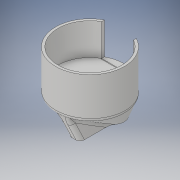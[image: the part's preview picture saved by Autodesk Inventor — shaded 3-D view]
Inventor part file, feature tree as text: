
AUTODESK INVENTOR PART (.ipt)
format: ipt  version: 2019 (Build 230136000, 136)  size: 461,824 bytes
history: native  units: mm
features: sketch x7, extrude x5, fillet x5, loft x2, other x2, plane x1
ambient origin geometry x8: Origin, YZ Plane, XZ Plane, XY Plane, X Axis, Y Axis, Z Axis, Center Point
bodies: Solid1 (feature_tree)
feature tree (22):
  extrude  "Extrusion1"  Depth=86.0mm
  extrude  "Extrusion2"  Depth=1.0mm
  extrude  "Extrusion3"  Depth=40.0mm
  sketch  "Sketch9"  dims[d7=80.0mm d8=10.0mm d9=0.0mm]
  plane  "Work Plane2"
  loft  "Loft1"
  extrude  "Extrusion6"  Depth=40.0mm
  loft  "Loft2"
  fillet  "Fillet1"  [1 undecoded]
  fillet  "Fillet2"  Radius=20.0mm
  extrude  "Extrusion8"  TaperAngle=0.0deg  [1 undecoded]
  fillet  "Fillet4"  [1 undecoded]
  fillet  "Fillet5"  Radius=10.0mm
  fillet  "Fillet6"  Radius=10.0mm
  sketch  "Sketch1"  dims[d0=80.0mm d1=86.0mm]
  sketch  "Sketch2"  dims[d2=40.0mm d3=0.0mm d4=1.0mm]
  sketch  "Sketch3"  dims[d5=1.0mm d6=40.0mm]
  sketch  "Sketch10"  dims[d10=10.0mm d11=0.0mm d21=40.0mm]
  sketch  "Sketch11"  dims[d22=26.0mm d23=0.0mm d24=90.0deg d25=0.0mm d26=90.0deg d27=20.0mm]
  other  "Edges1"
  other  "Edges2"
  sketch  "Sketch12"  dims[d28=20.0mm d29=0.0mm d30=0.0mm d31=90.0deg d32=0.0mm d33=90.0deg d34=10.0mm d35=10.0mm d36=86.0mm d37=86.0mm d38=43.0mm d39=86.0mm d43=15.0mm d44=0.0mm d45=5.0mm d46=2.0mm d47=2.0mm]
note: 3 required parameter values undecoded (feature->parameter linkage not recoverable at this tier; creation-order binding heuristic only, values carry confidence <= 0.55)
